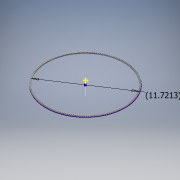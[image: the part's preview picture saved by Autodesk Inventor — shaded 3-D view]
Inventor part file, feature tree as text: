
AUTODESK INVENTOR PART (.ipt)
format: ipt  version: 2017 (Build 210142000, 142)  size: 2,403,328 bytes
history: native  units: mm
features: other x24, sketch x3, loft x2, pattern_circular x2, extrude x1
ambient origin geometry x6: Origin, XZ Plane, X Axis, Y Axis, Z Axis, Center Point
bodies: Solid1 (feature_tree)
feature tree (32):
  other  "Top Point"
  other  "Mesh Plane2"
  other  "Teeth Body"
  other  "Start Point"
  other  "Tooth Plane"
  other  "Start Sketch"
  other  "End Point"
  other  "3D Sketch Right"
  other  "End Plane Right"
  loft  "Loft Right"
  pattern_circular  "Circular Pattern Right"  [2 undecoded]
  other  "3D Sketch Left"
  other  "End Plane Left"
  loft  "Loft Left"
  pattern_circular  "Circular Pattern Left"  [2 undecoded]
  other  "Fix Body"
  extrude  "Extrusion1"  Depth=10.0mm
  sketch  "Sketch9"  dims[d3=5.08mm d4=8.681765mm d5=90.0deg d7=925.768798mm d8=848.473196mm d9=1817.033254mm d11=5.266267mm d12=894.052839mm d15=819.405312mm d16=1754.783423mm d17=0.0mm d18=90.0deg d19=0.0mm d20=90.0deg d21=1760.0mm d22=360.0deg d26=126.354884mm d27=0.358232mm d28=298.026667mm d29=-15.027199mm d30=894.052839mm d31=819.405312mm d32=1754.783423mm d35=0.0mm d37=0.0mm d39=0.0mm d40=90.0deg d41=1760.0mm d42=360.0deg d46=90.0deg d47=90.0deg d48=0.0mm d49=0.0mm d50=90.0deg d51=0.1785mm d52=0.0mm d53=0.0mm d54=0.0mm d56=9.853856mm d57=2193.202266mm d58=2187.912293mm d59=2118.065243mm d60=2112.956499mm d61=2118.065243mm d62=2112.956499mm d63=90.0deg d64=90.0deg d65=126.354884mm d66=31.5mm d67=298.026667mm d68=-15.027199mm d69=0.358232mm d70=819.405312mm d71=1754.783423mm d72=894.052839mm d73=2112.956499mm d74=2118.065243mm d75=0.0mm d76=90.0deg d77=0.0mm d78=90.0deg d79=0.0mm d80=90.0deg d81=1760.0mm d82=360.0deg d84=10.0mm d85=20.0mm d86=20.0mm d87=10.0mm d88=0.0mm d89=0.0mm d91=25.4mm d92=0.0mm]
  other  "Mesh Plane"
  other  "Top Plane"
  other  "Teeth Body Sketch"
  other  "End Plane"
  other  "End Sketch"
  other  "Helical Curve Left"
  other  "End Sketch Left"
  other  "Body Sketch"
  sketch  "Sketch6"  dims[d0=298.026667mm d1=297.721421mm]
  other  "Srf1"
  other  "Helical Curve Right"
  other  "End Sketch Right"
  sketch  "Sketch8"  dims[d2=298.228244mm]
  other  "Pitch Diameter"
note: 4 required parameter values undecoded (feature->parameter linkage not recoverable at this tier; creation-order binding heuristic only, values carry confidence <= 0.55)
